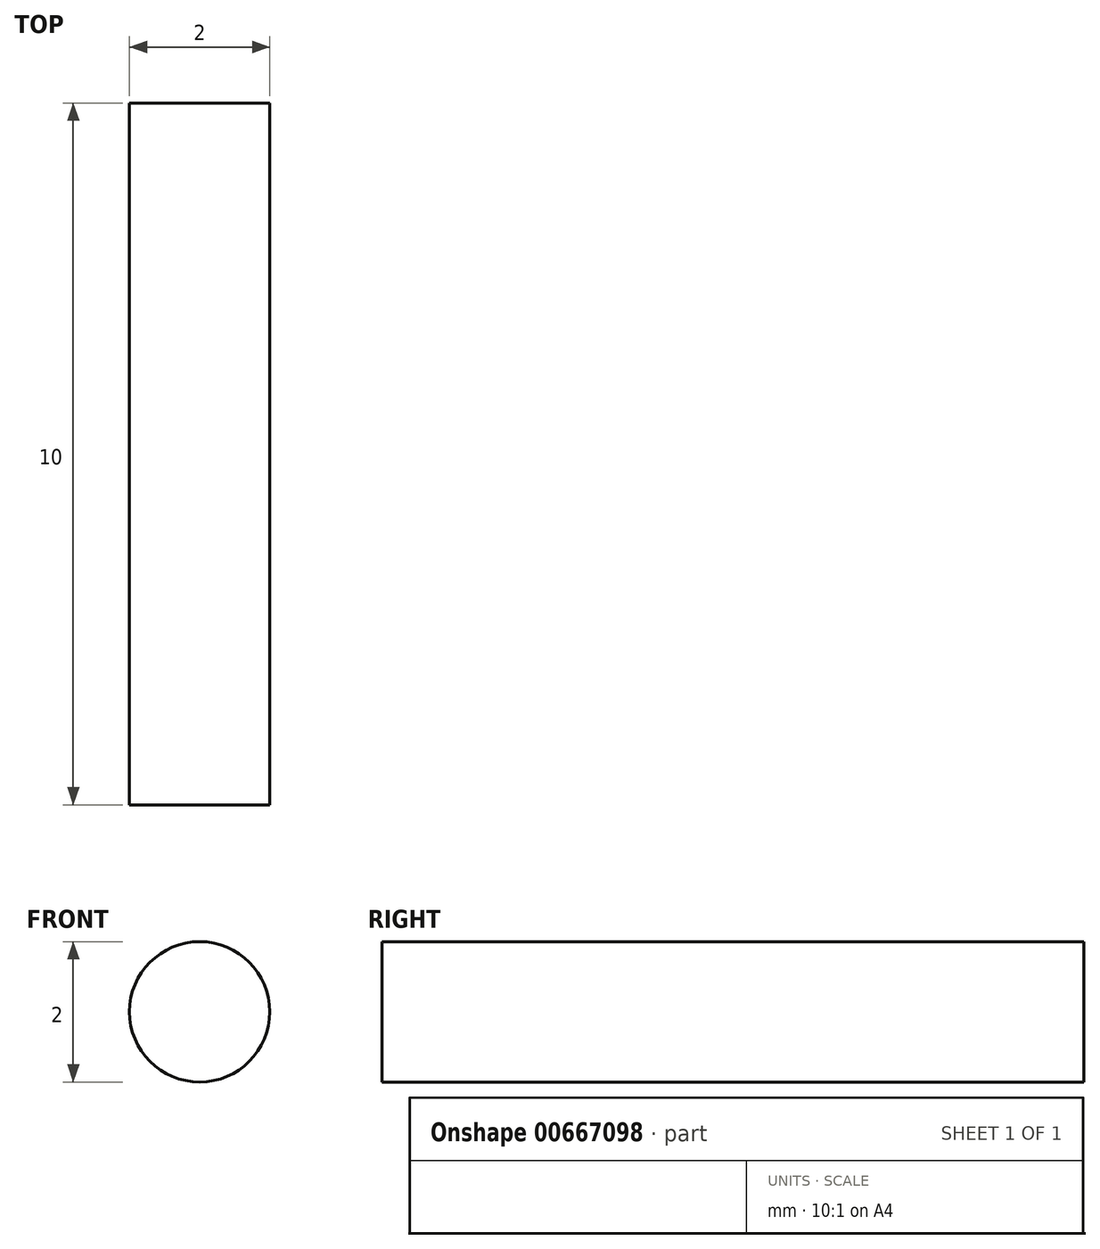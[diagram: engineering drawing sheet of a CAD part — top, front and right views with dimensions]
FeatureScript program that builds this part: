
annotation { "Feature Type Name" : "Feature", "Feature Type Description" : "" }
export const myFeature = defineFeature(function(context is Context, id is Id, definition is map)
    precondition{}
    {
        {
            var Q0;
            Q0=qCreatedBy(makeId("Front.planeOp"),FACE);
            var sketch = newSketch(context, id + "F0", { "sketchPlane" : qUnion([Q0])});
            skCircle(sketch, "E0", {"center": v(0, 0) * mm, "radius": 1 * mm});
            skSolve(sketch);
        }
        {
            var Q0;
            Q0=makeQuery(id+"F0.imprint","IMPRINT",FACE,{"disambiguationData":[TD([[makeQuery(id+"F0.imprint","IMPRINT",EDGE,{"derivedFrom":sQuery(id+"F0.wireOp",EDGE,"E0")}),1.0]])]});
            extrude(context, id + "F1", {"entities" : qUnion([Q0]), "endBound" : BoundingType.SYMMETRIC, "depth" : 10 * mm, "offsetDistance" : 25 * mm});
        }
    });
